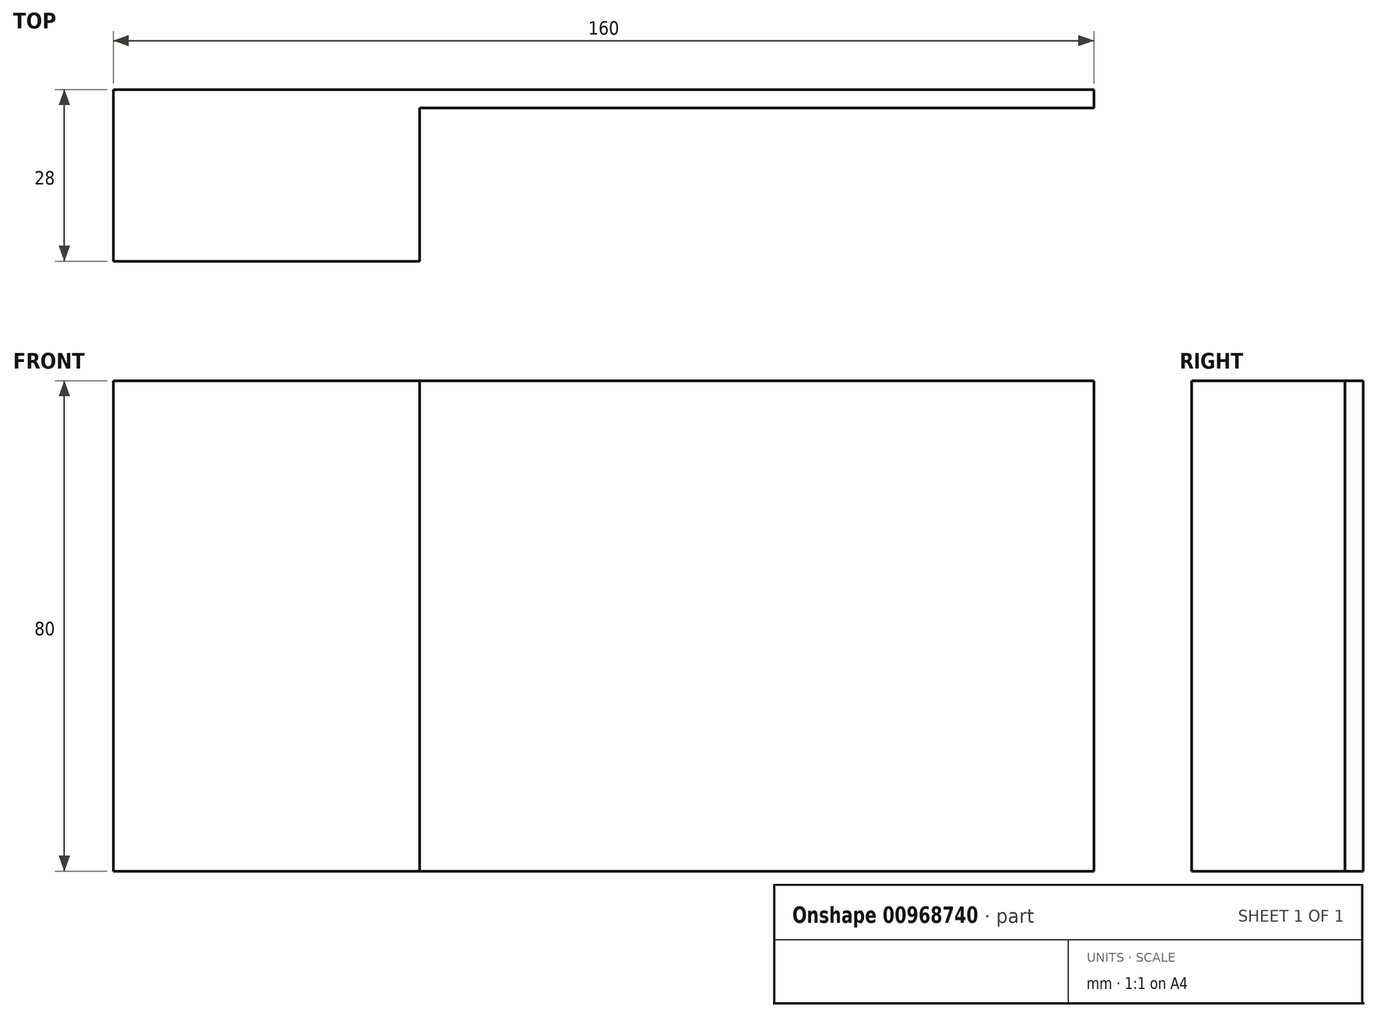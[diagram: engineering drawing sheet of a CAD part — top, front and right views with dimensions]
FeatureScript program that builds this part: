
annotation { "Feature Type Name" : "Feature", "Feature Type Description" : "" }
export const myFeature = defineFeature(function(context is Context, id is Id, definition is map)
    precondition{}
    {
        {
            var Q0;
            Q0=qCreatedBy(makeId("Front.planeOp"),FACE);
            var sketch = newSketch(context, id + "F0", { "sketchPlane" : qUnion([Q0])});
            skLineSegment(sketch, "E0.bottom", {"start": v(-80, 40) * mm, "end": v(80, 40) * mm});
            skLineSegment(sketch, "E0.top", {"start": v(-80, -40) * mm, "end": v(80, -40) * mm});
            skLineSegment(sketch, "E0.left", {"start": v(-80, 40) * mm, "end": v(-80, -40) * mm});
            skLineSegment(sketch, "E0.right", {"start": v(80, 40) * mm, "end": v(80, -40) * mm});
            skSolve(sketch);
        }
        {
            var Q0;
            Q0=makeQuery(id+"F0.imprint","IMPRINT",FACE,{"disambiguationData":[TD([[makeQuery(id+"F0.imprint","IMPRINT",EDGE,{"derivedFrom":sQuery(id+"F0.wireOp",EDGE,"E0.bottom")}),-1.0]])]});
            extrude(context, id + "F1", {"entities" : qUnion([Q0]), "depth" : 3 * mm, "offsetDistance" : 25 * mm});
        }
        {
            var Q0;
            Q0=makeQuery(id+"F1.opExtrude","CAP_FACE",FACE,{"disambiguationData":[OSD([sQuery(id+"F0.wireOp",EDGE,"E0.bottom"),sQuery(id+"F0.wireOp",EDGE,"E0.top"),sQuery(id+"F0.wireOp",EDGE,"E0.left"),sQuery(id+"F0.wireOp",EDGE,"E0.right")])],"isStart":false});
            var sketch = newSketch(context, id + "F2", { "sketchPlane" : qUnion([Q0])});
            skLineSegment(sketch, "E1.0", {"start": v(-80, 40) * mm, "end": v(-30, 40) * mm});
            skLineSegment(sketch, "E2.0", {"start": v(-80, 40) * mm, "end": v(-80, -40) * mm});
            skLineSegment(sketch, "E3.0", {"start": v(-80, -40) * mm, "end": v(-30, -40) * mm});
            skLineSegment(sketch, "E4", {"start": v(-30, 40) * mm, "end": v(-30, -40) * mm});
            skPoint(sketch, "E5.orphan", {"position": v(80, 40) * mm});
            skPoint(sketch, "E6.orphan", {"position": v(80, -40) * mm});
            skSolve(sketch);
        }
        {
            var Q0;
            Q0=makeQuery(id+"F2.imprint","IMPRINT",FACE,{"disambiguationData":[TD([[makeQuery(id+"F2.imprint","IMPRINT",EDGE,{"derivedFrom":sQuery(id+"F2.wireOp",EDGE,"E1.0")}),-1.0]])]});
            extrude(context, id + "F3", {"entities" : qUnion([Q0]), "operationType" : NewBodyOperationType.ADD, "depth" : 25 * mm, "offsetDistance" : 25 * mm});
        }
    });
